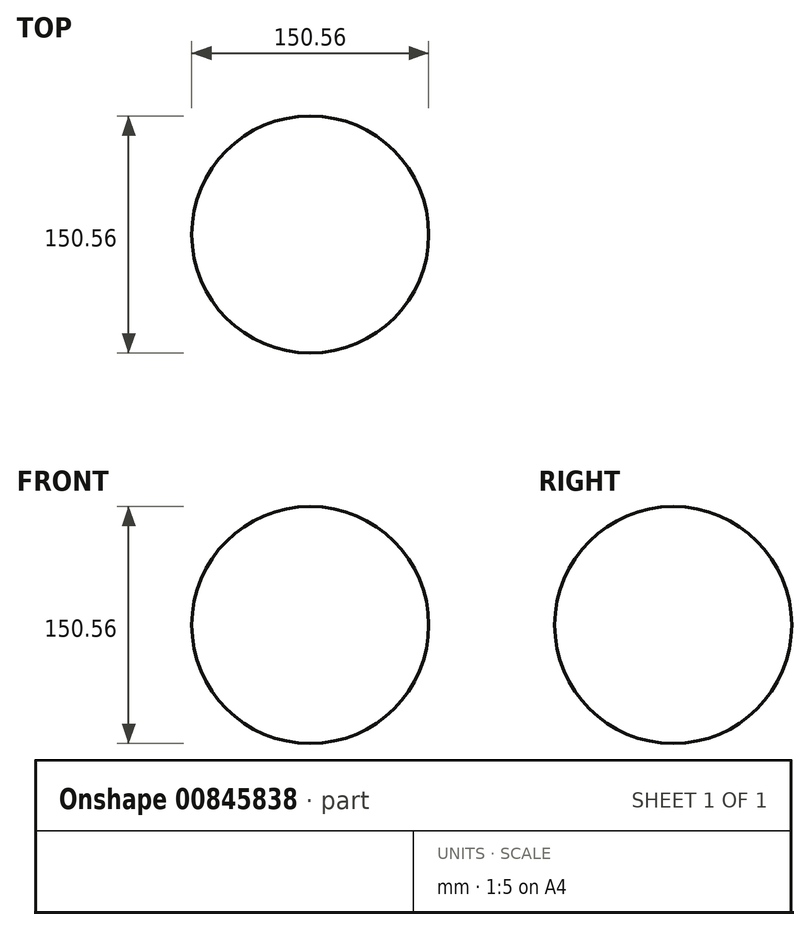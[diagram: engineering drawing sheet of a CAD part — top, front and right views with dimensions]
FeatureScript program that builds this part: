
annotation { "Feature Type Name" : "Feature", "Feature Type Description" : "" }
export const myFeature = defineFeature(function(context is Context, id is Id, definition is map)
    precondition{}
    {
        {
            var Q0;
            Q0=qCreatedBy(makeId("Front.planeOp"),FACE);
            var sketch = newSketch(context, id + "F0", { "sketchPlane" : qUnion([Q0])});
            skCircle(sketch, "E0", {"center": v(0, 0) * mm, "radius": 75.28 * mm});
            skLineSegment(sketch, "E1", {"start": v(0, -75.28) * mm, "end": v(0, 75.28) * mm});
            skSolve(sketch);
        }
        {
            var Q0;
            {var subQ0=sQuery(id+"F0.wireOp",EDGE,"E1");Q0=makeQuery(id+"F0.imprint","IMPRINT",FACE,{"disambiguationData":[TD([[makeQuery(id+"F0.imprint","IMPRINT",EDGE,{"derivedFrom":subQ0}),1.0]])]});}
            var Q1;
            Q1=sQuery(id+"F0.wireOp",EDGE,"E1");
            revolve(context, id + "F1", {"surfaceOperationType" : NewSurfaceOperationType.NEW, "entities" : qUnion([Q0]), "axis" : qUnion([Q1]), "revolveType" : RevolveType.FULL});
        }
    });
